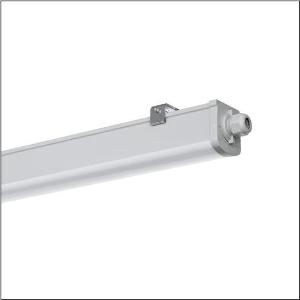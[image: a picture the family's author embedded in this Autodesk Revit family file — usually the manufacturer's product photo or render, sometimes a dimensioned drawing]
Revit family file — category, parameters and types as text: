
# Revit family: monsun_r__31_51fa20dk450b_5819
name_source: partatom
category: Lighting Fixtures
units: mm (PartAtom-declared; Revit-internal decimal feet)

## family parameters
Cut with Voids When Loaded = No
Host = Face
Light Source = No
Part Type = Normal
Room Calculation Point = No
Round Connector Dimension = Use Diameter
Shared = No

## types (1)
- Monsun® 31 (1 x LED, 5100 lm, 38 W, 4000K)
    Apparent Load = 38 VA
    CIE Flux Codes = 42 72 91 92 100
    Color Rendering = 80
    Color Temperature = 4000K
    Default Elevation = 1800 mm
    Description = Monsun® 31, damp-proof luminaire, primary optical cover: diffuser, of PC, frosted, light emission: direct distribution, primary light characteristic: symmetric, installation type: surface-mounted, LED, rated luminous flux: 5.100lm, luminous efficacy: 134lm/W, light colour: 840, colour temperature: 4000K, control gear: ECG, with terminal, 5+1-pole, max. 2.5mm², through-wiring: 3x 2.5mm² + 3x 1.5mm², mains connection: 220..240V, AC, 50/60Hz, rated input power: 38W, housing, luminaire housing, of PC, light grey (RAL 7035), length: 1.158mm, width: 68mm, height: 76mm, protection rating (complete): IP66, insulation class (complete): insulation class II (safety insulation), certification: CE, ENEC, UKCA, protection symbol: D, impact resistance: IK08, permissible operating ambient temperature: -20..+40°C, corresponds to IFS (International Featured Standards) requirements for safety and quality in the food industry, contact your sales advisor before using the luminaires in applications with unclear chemical exposure, large temperature fluctuations or condensation-forming humidity, packaging unit: 1 piece
    Height = 77 mm
    Lamp = 1 x LED
    Lamp Light Flux = 5100 lm
    Lamp Power = 38 W
    Lamp count = 1
    Length = 1218 mm
    Luminous efficacy = 134 lm/W
    Manufacturer = Siteco
    ModVariant = No
    Model = 51FA20DK450B
    Mounting Place = Ceiling
    Mounting Type = Surface mounted
    Number of Poles = 1
    OnlyDefault = Yes
    Power Factor = 1
    Product Name = Monsun® 31
    Product group = damp-proof luminaire
    ProductGroupID = 300
    Protection Class = Protection class II
    Protection Degree = IP 66
    RLX_Detail_Level = 1
    RLX_Emergency_Light_Flux = 0 lm
    RLX_Emergency_Type = 0
    RLX_Emergency_Type_DB = No
    RlxData = <blob elided: 33017 chars, md5=4c65e7f0>
    Socket = socket
    Standby Power = 0 W
    System Light Flux = 5100 lm
    System Power = 38 W
    Type Comments = Product without accessories
    Type Image = l_1006174.jpg
    URL = http://relux.com
    VarID = ---
    Voltage = 0 V
    Weight = 0.00 kg
    Width = 69 mm

## geometry (parser evidence)
native form markers: Blend x4, Sweep x12
no freeform markers — native parametric forms only
